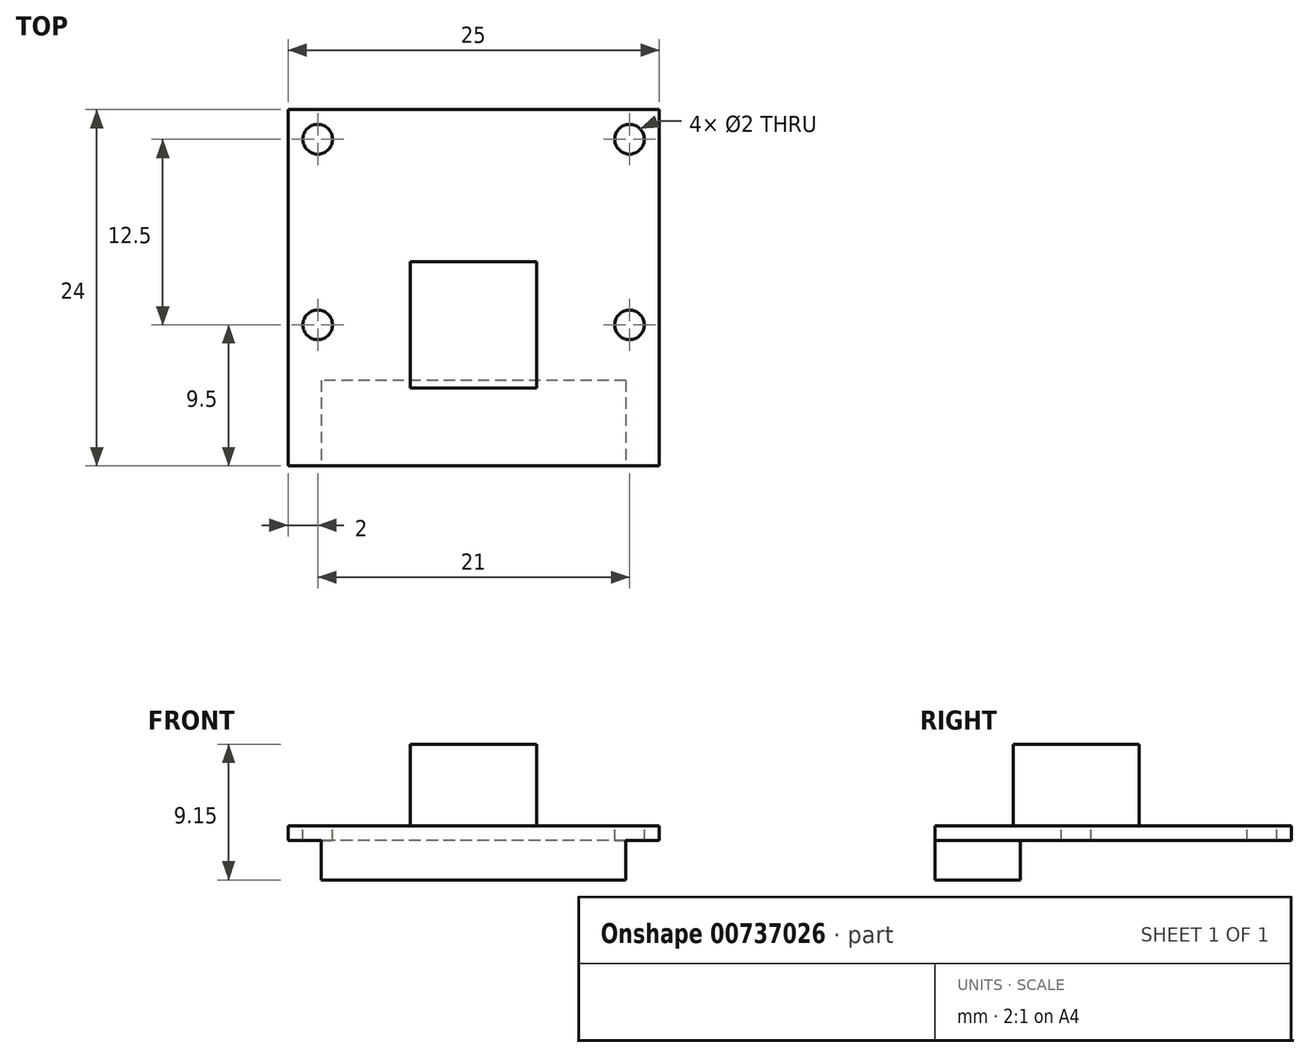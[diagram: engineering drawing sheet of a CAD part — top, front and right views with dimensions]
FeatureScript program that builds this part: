
annotation { "Feature Type Name" : "Feature", "Feature Type Description" : "" }
export const myFeature = defineFeature(function(context is Context, id is Id, definition is map)
    precondition{}
    {
        {
            var Q0;
            Q0=qCreatedBy(makeId("Top.planeOp"),FACE);
            var sketch = newSketch(context, id + "F0", { "sketchPlane" : qUnion([Q0])});
            skLineSegment(sketch, "E0.bottom", {"start": v(12.5, 12) * mm, "end": v(-12.5, 12) * mm});
            skLineSegment(sketch, "E0.top", {"start": v(12.5, -12) * mm, "end": v(-12.5, -12) * mm});
            skLineSegment(sketch, "E0.left", {"start": v(12.5, 12) * mm, "end": v(12.5, -12) * mm});
            skLineSegment(sketch, "E0.right", {"start": v(-12.5, 12) * mm, "end": v(-12.5, -12) * mm});
            skPoint(sketch, "E0.middle", {"position": v(0, 0) * mm});
            skCircle(sketch, "E1", {"center": v(-10.5, -2.5) * mm, "radius": 1 * mm});
            skCircle(sketch, "E2", {"center": v(10.5, -2.5) * mm, "radius": 1 * mm});
            skCircle(sketch, "E3", {"center": v(-10.5, 10) * mm, "radius": 1 * mm});
            skCircle(sketch, "E4", {"center": v(10.5, 10) * mm, "radius": 1 * mm});
            skLineSegment(sketch, "E5.bottom", {"start": v(4.25, 1.75) * mm, "end": v(-4.25, 1.75) * mm});
            skLineSegment(sketch, "E5.top", {"start": v(4.25, -6.75) * mm, "end": v(-4.25, -6.75) * mm});
            skLineSegment(sketch, "E5.left", {"start": v(4.25, 1.75) * mm, "end": v(4.25, -6.75) * mm});
            skLineSegment(sketch, "E5.right", {"start": v(-4.25, 1.75) * mm, "end": v(-4.25, -6.75) * mm});
            skPoint(sketch, "E5.middle", {"position": v(0, -2.5) * mm});
            skLineSegment(sketch, "E6.bottom", {"start": v(10.25, -6.25) * mm, "end": v(-10.25, -6.25) * mm});
            skLineSegment(sketch, "E6.top", {"start": v(10.25, -12) * mm, "end": v(-10.25, -12) * mm});
            skLineSegment(sketch, "E6.left", {"start": v(10.25, -6.25) * mm, "end": v(10.25, -12) * mm});
            skLineSegment(sketch, "E6.right", {"start": v(-10.25, -6.25) * mm, "end": v(-10.25, -12) * mm});
            skPoint(sketch, "E6.middle", {"position": v(0, -9.13) * mm});
            skSolve(sketch);
        }
        {
            var Q0;
            Q0 = qSketchRegion(id + "F0", true);
            var Q1;
            {var subQ0=sQuery(id+"F0.wireOp",EDGE,"E5.bottom");Q1=makeQuery(id+"F0.imprint","IMPRINT",FACE,{"disambiguationData":[TD([[makeQuery(id+"F0.imprint","IMPRINT",EDGE,{"derivedFrom":subQ0}),1.0]])]});}
            var Q2;
            {var subQ0=sQuery(id+"F0.wireOp",EDGE,"E5.top");Q2=makeQuery(id+"F0.imprint","IMPRINT",FACE,{"disambiguationData":[TD([[makeQuery(id+"F0.imprint","IMPRINT",EDGE,{"derivedFrom":subQ0}),-1.0]])]});}
            extrude(context, id + "F1", {"entities" : qUnion([Q0, Q1, Q2]), "oppositeDirection" : true, "depth" : 1 * mm, "offsetDistance" : 25 * mm});
        }
        {
            var Q0;
            {var subQ1=sQuery(id+"F0.wireOp",EDGE,"E5.top");Q0=makeQuery(id+"F0.imprint","IMPRINT",FACE,{"disambiguationData":[TD([[makeQuery(id+"F0.imprint","IMPRINT",EDGE,{"derivedFrom":subQ1}),1.0]])]});}
            var Q1;
            {var subQ0=sQuery(id+"F0.wireOp",EDGE,"E5.top");Q1=makeQuery(id+"F0.imprint","IMPRINT",FACE,{"disambiguationData":[TD([[makeQuery(id+"F0.imprint","IMPRINT",EDGE,{"derivedFrom":subQ0}),-1.0]])]});}
            extrude(context, id + "F2", {"entities" : qUnion([Q0, Q1]), "operationType" : NewBodyOperationType.ADD, "oppositeDirection" : true, "depth" : 3.65 * mm, "offsetDistance" : 25 * mm});
        }
        {
            var Q0;
            {var subQ0=sQuery(id+"F0.wireOp",EDGE,"E5.bottom");Q0=makeQuery(id+"F0.imprint","IMPRINT",FACE,{"disambiguationData":[TD([[makeQuery(id+"F0.imprint","IMPRINT",EDGE,{"derivedFrom":subQ0}),1.0]])]});}
            var Q1;
            {var subQ0=sQuery(id+"F0.wireOp",EDGE,"E5.top");Q1=makeQuery(id+"F0.imprint","IMPRINT",FACE,{"disambiguationData":[TD([[makeQuery(id+"F0.imprint","IMPRINT",EDGE,{"derivedFrom":subQ0}),-1.0]])]});}
            extrude(context, id + "F3", {"entities" : qUnion([Q0, Q1]), "operationType" : NewBodyOperationType.ADD, "depth" : 5.5 * mm, "offsetDistance" : 25 * mm});
        }
    });
